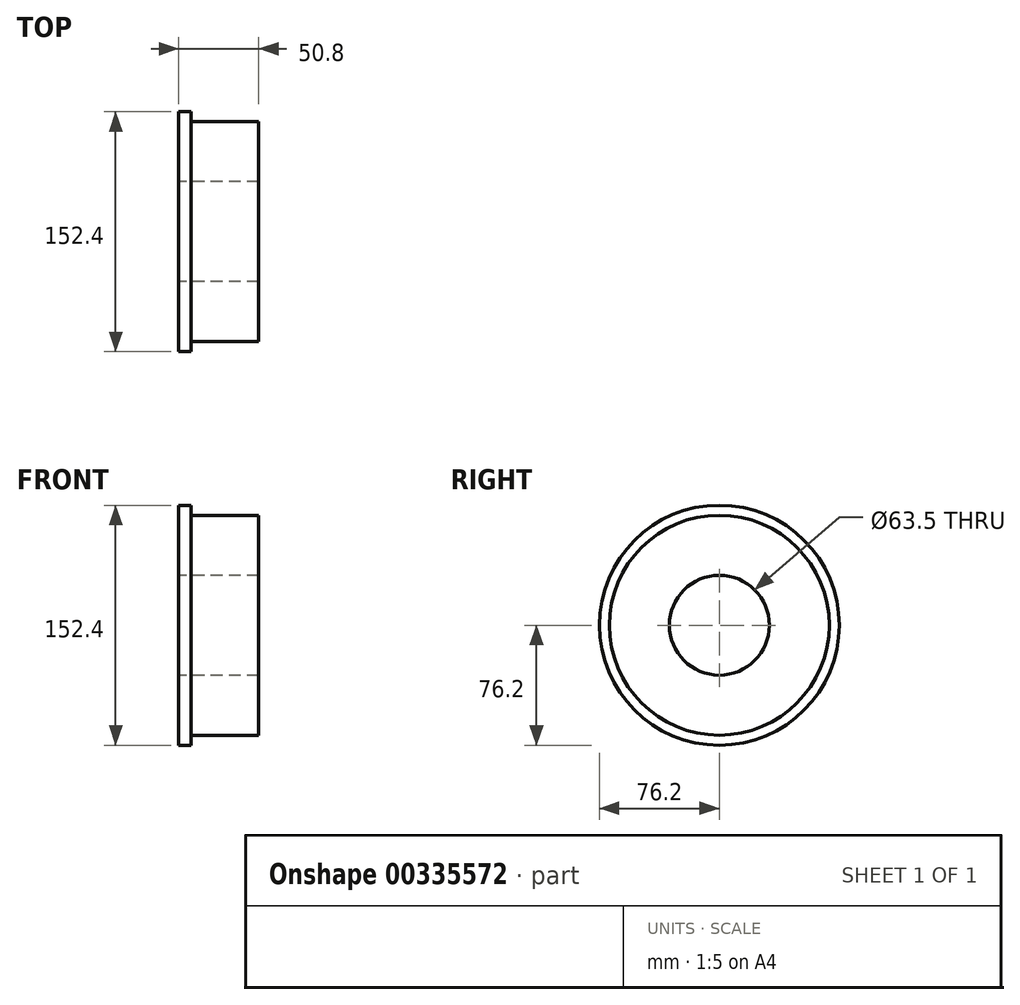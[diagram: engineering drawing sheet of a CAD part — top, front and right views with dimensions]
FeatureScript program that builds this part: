
annotation { "Feature Type Name" : "Feature", "Feature Type Description" : "" }
export const myFeature = defineFeature(function(context is Context, id is Id, definition is map)
    precondition{}
    {
        {
            var Q0;
            Q0=qCreatedBy(makeId("Right.planeOp"),FACE);
            var sketch = newSketch(context, id + "F0", { "sketchPlane" : qUnion([Q0])});
            skCircle(sketch, "E0", {"center": v(0, 0) * mm, "radius": 69.85 * mm});
            skCircle(sketch, "E1", {"center": v(0, 0) * mm, "radius": 31.75 * mm});
            skSolve(sketch);
        }
        {
            var Q0;
            Q0=qSketchRegion(id+"F0",true);
            extrude(context, id + "F1", {"entities" : qUnion([Q0]), "depth" : 42.93 * mm});
        }
        {
            var Q0;
            Q0=makeQuery(id+"F1.opExtrude","CAP_FACE",FACE,{"disambiguationData":[OSD([sQuery(id+"F0.wireOp",EDGE,"E0"),sQuery(id+"F0.wireOp",EDGE,"E1")])],"isStart":true});
            var sketch = newSketch(context, id + "F2", { "sketchPlane" : qUnion([Q0])});
            skCircle(sketch, "E2", {"center": v(0, 0) * mm, "radius": 76.2 * mm});
            skCircle(sketch, "E3.0", {"center": v(0, 0) * mm, "radius": 31.75 * mm});
            skSolve(sketch);
        }
        {
            var Q0;
            Q0=qSketchRegion(id+"F2",true);
            extrude(context, id + "F3", {"entities" : qUnion([Q0]), "operationType" : NewBodyOperationType.ADD, "depth" : 7.87 * mm});
        }
    });
